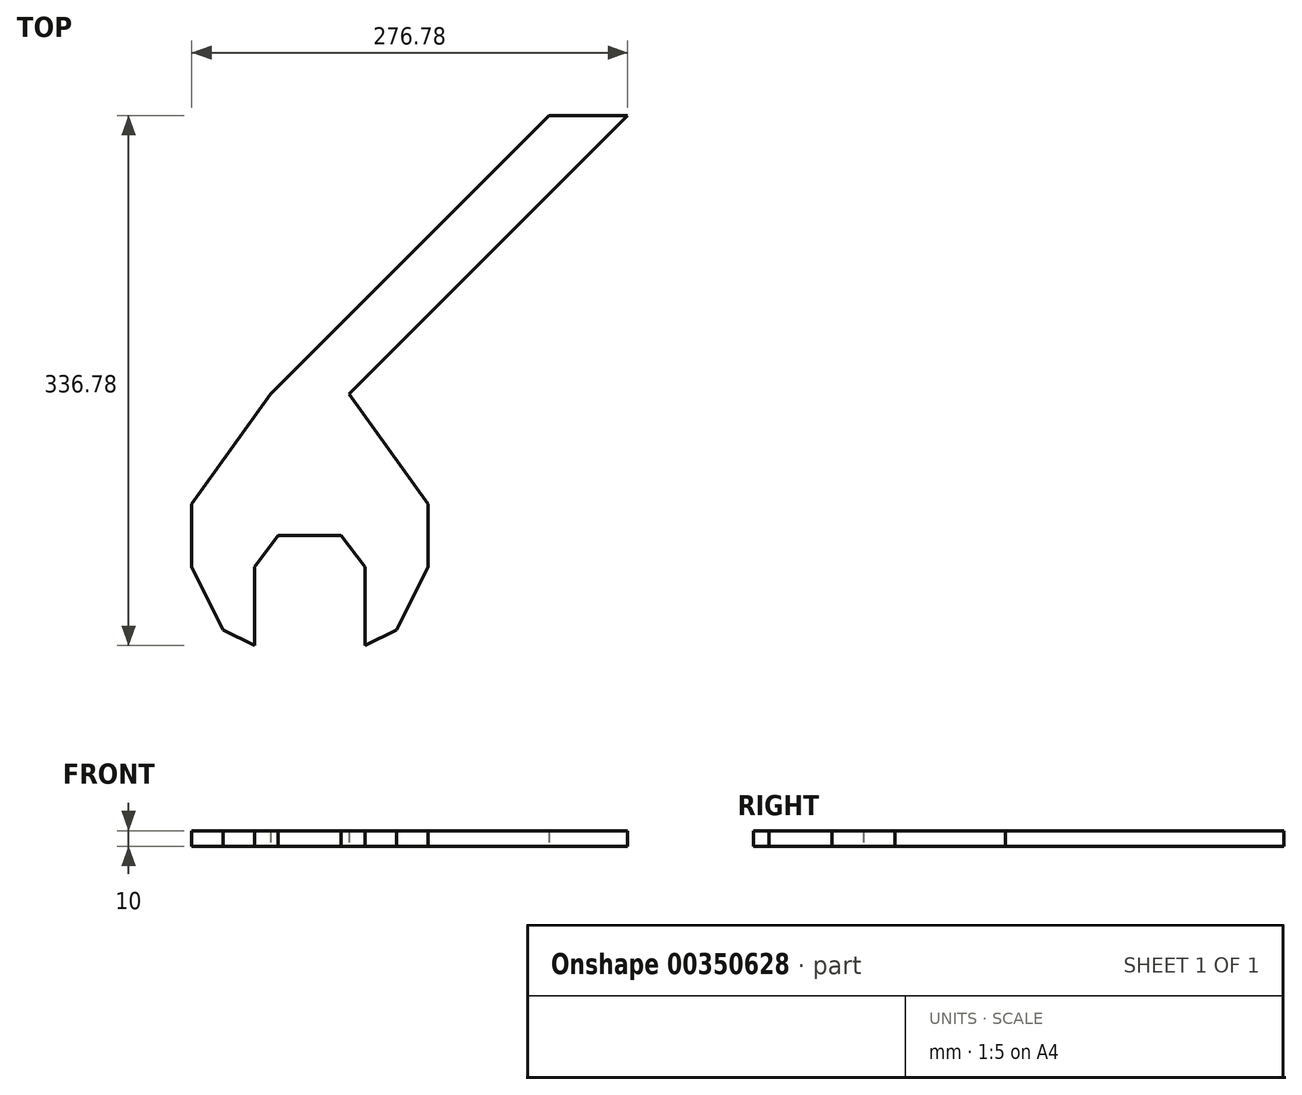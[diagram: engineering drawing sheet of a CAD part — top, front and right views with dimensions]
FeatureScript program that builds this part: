
annotation { "Feature Type Name" : "Feature", "Feature Type Description" : "" }
export const myFeature = defineFeature(function(context is Context, id is Id, definition is map)
    precondition{}
    {
        {
            var Q0;
            Q0=qCreatedBy(makeId("Top.planeOp"),FACE);
            var sketch = newSketch(context, id + "F0", { "sketchPlane" : qUnion([Q0])});
            skLineSegment(sketch, "E0", {"start": v(-20, 0) * mm, "end": v(20, 0) * mm});
            skLineSegment(sketch, "E1", {"start": v(-20, 0) * mm, "end": v(-35, -20) * mm});
            skLineSegment(sketch, "E2", {"start": v(-35, -20) * mm, "end": v(-35, -70) * mm});
            skLineSegment(sketch, "E3", {"start": v(0, 0) * mm, "end": v(0, -67.64) * mm, "construction": true});
            skLineSegment(sketch, "E4.MirrorCS", {"start": v(20, 0) * mm, "end": v(35, -20) * mm});
            skLineSegment(sketch, "E5.MirrorCS", {"start": v(35, -20) * mm, "end": v(35, -70) * mm});
            skLineSegment(sketch, "E6", {"start": v(-35, -70) * mm, "end": v(-55, -60) * mm});
            skLineSegment(sketch, "E7", {"start": v(-55, -60) * mm, "end": v(-75, -20) * mm});
            skLineSegment(sketch, "E8", {"start": v(-75, -20) * mm, "end": v(-75, 20) * mm});
            skLineSegment(sketch, "E9", {"start": v(-75, 20) * mm, "end": v(-25, 90) * mm});
            skLineSegment(sketch, "E10.MirrorCS", {"start": v(35, -70) * mm, "end": v(55, -60) * mm});
            skLineSegment(sketch, "E11.MirrorCS", {"start": v(55, -60) * mm, "end": v(75, -20) * mm});
            skLineSegment(sketch, "E12.MirrorCS", {"start": v(75, 20) * mm, "end": v(25, 90) * mm});
            skLineSegment(sketch, "E13.MirrorCS", {"start": v(75, -20) * mm, "end": v(75, 20) * mm});
            skLineSegment(sketch, "E14", {"start": v(-25, 90) * mm, "end": v(151.78, 266.78) * mm});
            skLineSegment(sketch, "E15", {"start": v(151.78, 266.78) * mm, "end": v(201.78, 266.78) * mm});
            skLineSegment(sketch, "E16", {"start": v(201.78, 266.78) * mm, "end": v(25, 90) * mm});
            skLineSegment(sketch, "E17", {"start": v(25, 90) * mm, "end": v(157.59, 90) * mm, "construction": true});
            skSolve(sketch);
        }
        {
            var Q0;
            Q0=makeQuery(id+"F0.imprint","IMPRINT",FACE,{"disambiguationData":[TD([[makeQuery(id+"F0.imprint","IMPRINT",EDGE,{"derivedFrom":sQuery(id+"F0.wireOp",EDGE,"E0")}),1.0]])]});
            extrude(context, id + "F1", {"entities" : qUnion([Q0]), "depth" : 10 * mm});
        }
    });
